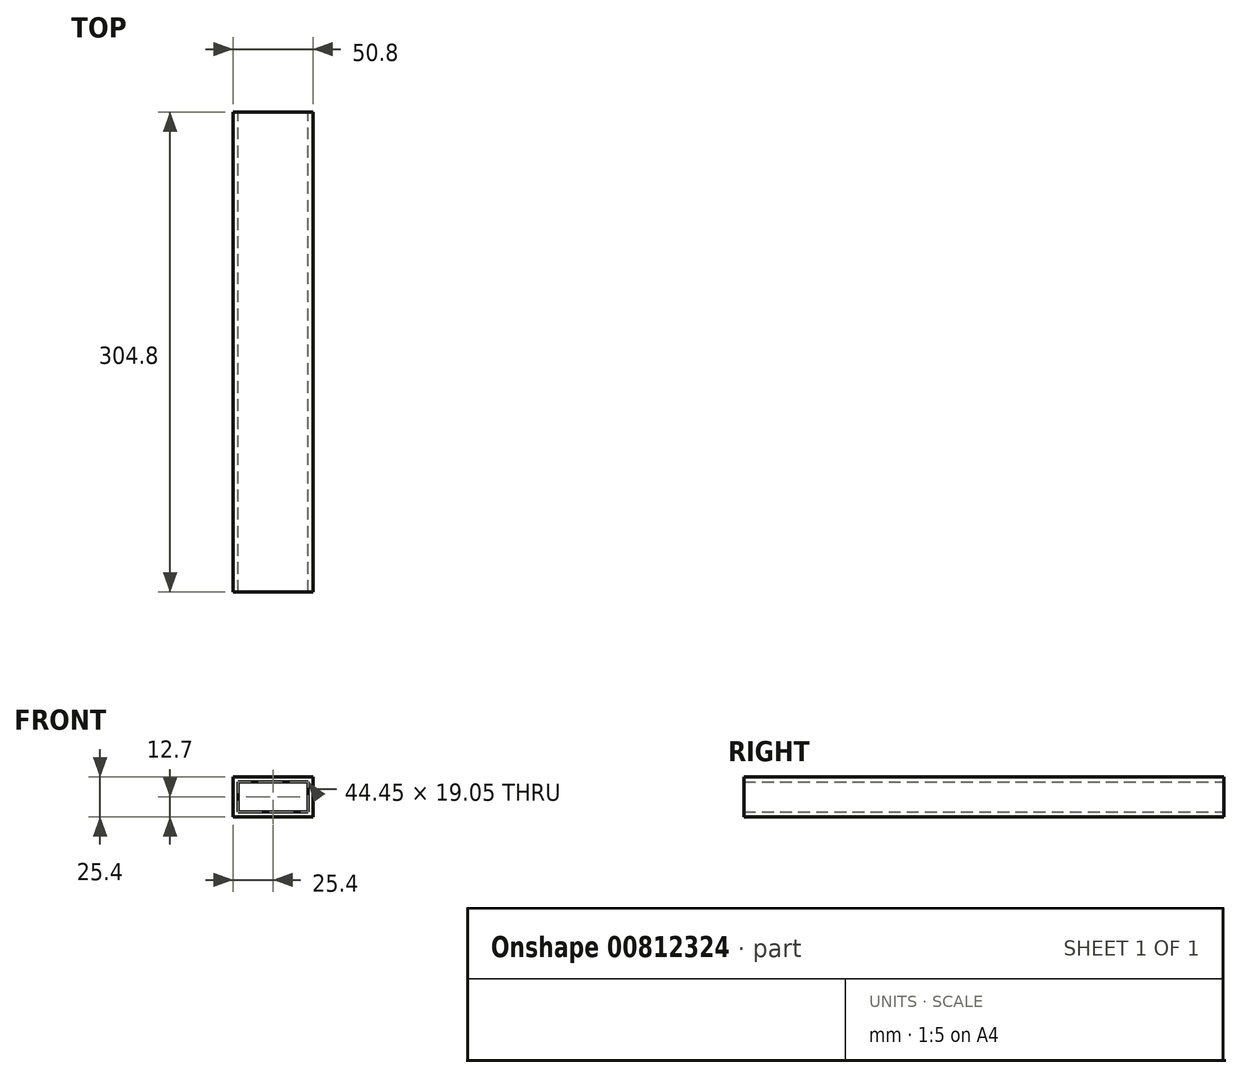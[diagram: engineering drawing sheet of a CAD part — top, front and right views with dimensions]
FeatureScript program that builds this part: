
annotation { "Feature Type Name" : "Feature", "Feature Type Description" : "" }
export const myFeature = defineFeature(function(context is Context, id is Id, definition is map)
    precondition{}
    {
        {
            var Q0;
            Q0=qCreatedBy(makeId("Front.planeOp"),FACE);
            var sketch = newSketch(context, id + "F0", { "sketchPlane" : qUnion([Q0])});
            skLineSegment(sketch, "E0.bottom", {"start": v(25.4, 12.7) * mm, "end": v(-25.4, 12.7) * mm});
            skLineSegment(sketch, "E0.top", {"start": v(25.4, -12.7) * mm, "end": v(-25.4, -12.7) * mm});
            skLineSegment(sketch, "E0.left", {"start": v(25.4, 12.7) * mm, "end": v(25.4, -12.7) * mm});
            skLineSegment(sketch, "E0.right", {"start": v(-25.4, 12.7) * mm, "end": v(-25.4, -12.7) * mm});
            skPoint(sketch, "E0.middle", {"position": v(0, 0) * mm});
            skLineSegment(sketch, "E1.bottom", {"start": v(22.23, 9.52) * mm, "end": v(-22.23, 9.52) * mm});
            skLineSegment(sketch, "E1.top", {"start": v(22.23, -9.52) * mm, "end": v(-22.23, -9.52) * mm});
            skLineSegment(sketch, "E1.left", {"start": v(22.23, 9.52) * mm, "end": v(22.23, -9.52) * mm});
            skLineSegment(sketch, "E1.right", {"start": v(-22.23, 9.52) * mm, "end": v(-22.23, -9.52) * mm});
            skSolve(sketch);
        }
        {
            var Q0;
            Q0 = qSketchRegion(id + "F0", true);
            extrude(context, id + "F1", {"entities" : qUnion([Q0]), "endBound" : BoundingType.SYMMETRIC, "depth" : 304.8 * mm, "offsetDistance" : 25.4 * mm});
        }
    });
